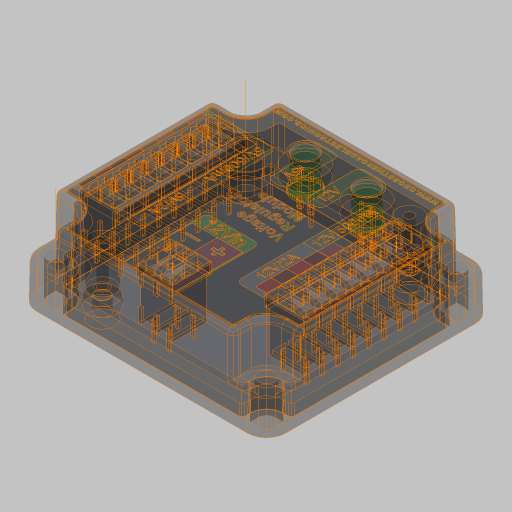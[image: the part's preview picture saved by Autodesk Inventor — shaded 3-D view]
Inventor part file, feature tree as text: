
AUTODESK INVENTOR PART (.ipt)
format: ipt  version: 2023.5 (Build 275446000, 446)  size: 6,884,864 bytes
history: native  units: in
note: dims shown in document units (in); Inventor stores cm internally (conversion verified against a paired STEP export)
features: other x6, plane x2
ambient origin geometry x8: Origin, YZ Plane, XZ Plane, XY Plane, X Axis, Y Axis, Z Axis, Center Point
bodies: Body1 (feature_tree), Body2 (feature_tree), Body3 (feature_tree), Body4 (feature_tree), Body5 (feature_tree), Body6 (feature_tree), Body7 (feature_tree), Body8 (feature_tree), Body9 (feature_tree), Body10 (feature_tree), Body11 (feature_tree), Body12 (feature_tree), Body13 (feature_tree), Body14 (feature_tree), Body15 (feature_tree), Body16 (feature_tree), Body17 (feature_tree), Body18 (feature_tree), Body19 (feature_tree), Body20 (feature_tree), Body21 (feature_tree), Body22 (feature_tree), Body23 (feature_tree), Body24 (feature_tree), Body25 (feature_tree), Body26 (feature_tree), Body27 (feature_tree), Body28 (feature_tree), Body29 (feature_tree), Body30 (feature_tree), Body31 (feature_tree), Body32 (feature_tree), Body33 (feature_tree), Body34 (feature_tree)
feature tree (8):
  other  "vrm1"
  other  "Work Axis2"
  plane  "Work Plane1"
  plane  "Work Plane2"
  other  "Work Axis1"
  other  "Work Axis3"
  other  "Composite1"
  other  "Srf1"
